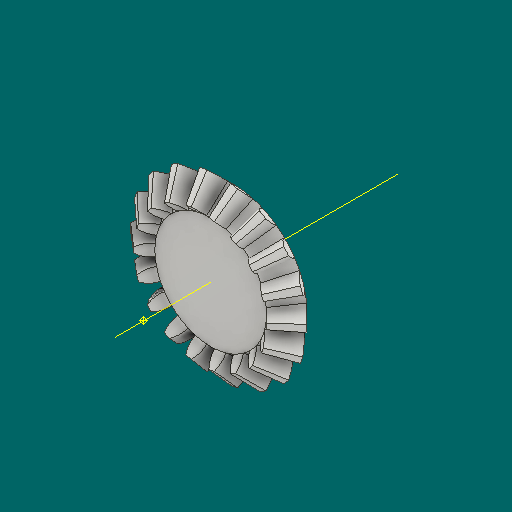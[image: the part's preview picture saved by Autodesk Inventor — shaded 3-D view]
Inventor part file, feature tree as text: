
AUTODESK INVENTOR PART (.ipt)
format: ipt  version: 2023.1 (Build 271208000, 208)  size: 494,080 bytes
history: native  units: mm
features: other x24, loft x2, pattern_circular x2, sketch x1
ambient origin geometry x6: Origin, XZ Plane, X Axis, Y Axis, Z Axis, Center Point
bodies: Solid1 (feature_tree)
feature tree (29):
  other  "Top Point"
  other  "Mesh Plane2"
  other  "Teeth Body"
  other  "Start Point"
  other  "Tooth Plane"
  other  "Start Sketch"
  other  "End Point"
  other  "3D Sketch Right"
  other  "End Plane Right"
  loft  "Loft Right"
  pattern_circular  "Circular Pattern Right"  [2 undecoded]
  other  "3D Sketch Left"
  other  "End Plane Left"
  loft  "Loft Left"
  pattern_circular  "Circular Pattern Left"  [2 undecoded]
  other  "Fix Body"
  other  "Mesh Plane"
  other  "Top Plane"
  other  "Teeth Body Sketch"
  other  "End Plane"
  other  "End Sketch"
  other  "Helical Curve Left"
  other  "End Sketch Left"
  other  "Body Sketch"
  sketch  "Sketch6"  dims[d0=22.86mm d1=20.704739mm d2=24.656051mm d3=4.0mm d4=10.531974mm d5=90.0deg d7=4.61849mm d8=5.357012mm d9=14.610805mm d11=4.1397mm d12=3.4357mm d15=3.985088mm d16=10.868995mm d17=0.0mm d18=90.0deg d19=0.0mm d20=90.0deg d21=180.0mm d22=360.0deg d26=70.487871mm d27=2.92721mm d28=22.86mm d29=-7.853982mm d30=3.4357mm d31=3.985088mm d32=10.868995mm d35=0.0mm d37=0.0mm d39=0.0mm d40=90.0deg d41=180.0mm d42=360.0deg d46=90.0deg d47=90.0deg d48=0.0mm d49=0.0mm d50=90.0deg d51=1.745329mm d52=0.0mm d53=0.0mm d54=0.0mm d56=6.566828mm d57=18.272661mm d58=14.305181mm d59=13.593054mm d60=10.641641mm d61=13.593054mm d62=10.641641mm d63=90.0deg d64=90.0deg d65=70.487871mm d66=31.5mm d67=22.86mm d68=-7.853982mm d69=2.92721mm d70=3.985088mm d71=10.868995mm d72=3.4357mm d73=10.641641mm d74=13.593054mm d75=0.0mm d76=90.0deg d77=0.0mm d78=90.0deg d79=0.0mm d80=90.0deg d81=180.0mm d82=360.0deg d84=10.0mm d85=20.0mm d86=20.0mm d87=10.0mm d88=0.0mm d89=0.0mm]
  other  "Srf1"
  other  "Helical Curve Right"
  other  "End Sketch Right"
  other  "Pitch Diameter"
note: 4 required parameter values undecoded (feature->parameter linkage not recoverable at this tier; creation-order binding heuristic only, values carry confidence <= 0.55)
